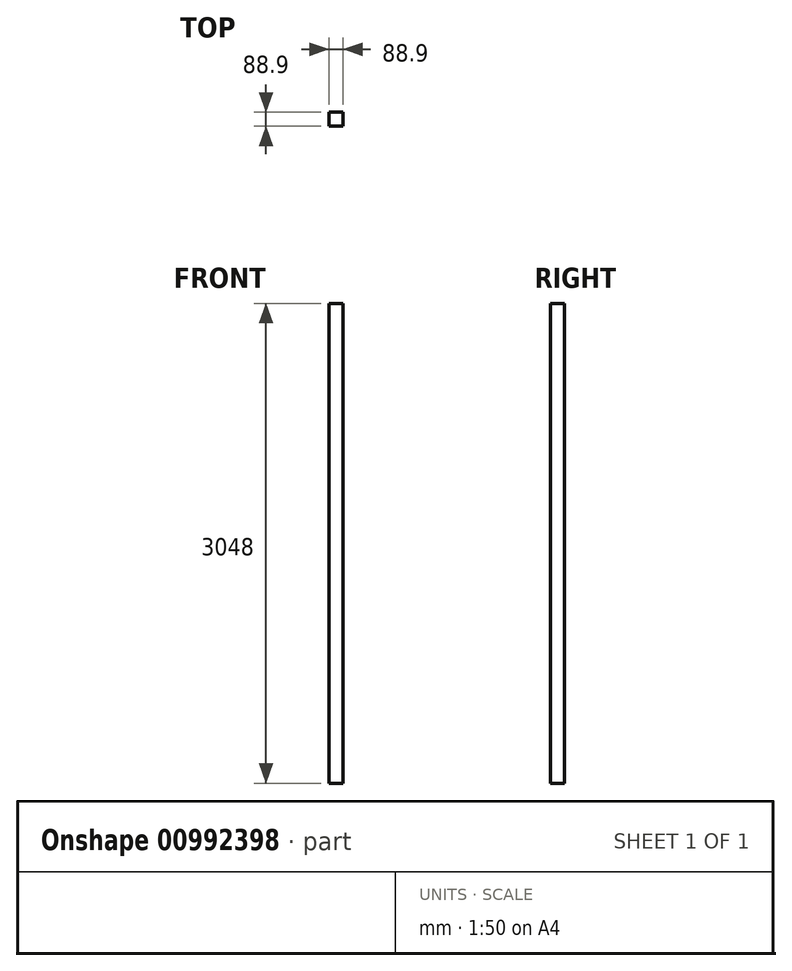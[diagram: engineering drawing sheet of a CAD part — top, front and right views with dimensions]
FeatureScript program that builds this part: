
annotation { "Feature Type Name" : "Feature", "Feature Type Description" : "" }
export const myFeature = defineFeature(function(context is Context, id is Id, definition is map)
    precondition{}
    {
        {
            var Q0;
            Q0=qCreatedBy(makeId("Top.planeOp"),FACE);
            var sketch = newSketch(context, id + "F0", { "sketchPlane" : qUnion([Q0])});
            skLineSegment(sketch, "E0.bottom", {"start": v(44.45, 44.45) * mm, "end": v(-44.45, 44.45) * mm});
            skLineSegment(sketch, "E0.top", {"start": v(44.45, -44.45) * mm, "end": v(-44.45, -44.45) * mm});
            skLineSegment(sketch, "E0.left", {"start": v(44.45, 44.45) * mm, "end": v(44.45, -44.45) * mm});
            skLineSegment(sketch, "E0.right", {"start": v(-44.45, 44.45) * mm, "end": v(-44.45, -44.45) * mm});
            skPoint(sketch, "E0.middle", {"position": v(0, 0) * mm});
            skSolve(sketch);
        }
        {
            var Q0;
            Q0 = qSketchRegion(id + "F0", true);
            extrude(context, id + "F1", {"entities" : qUnion([Q0]), "depth" : 2438.4 * mm, "offsetDistance" : 25.4 * mm, "hasSecondDirection" : true, "secondDirectionOppositeDirection" : true, "secondDirectionDepth" : 609.6 * mm});
        }
    });
